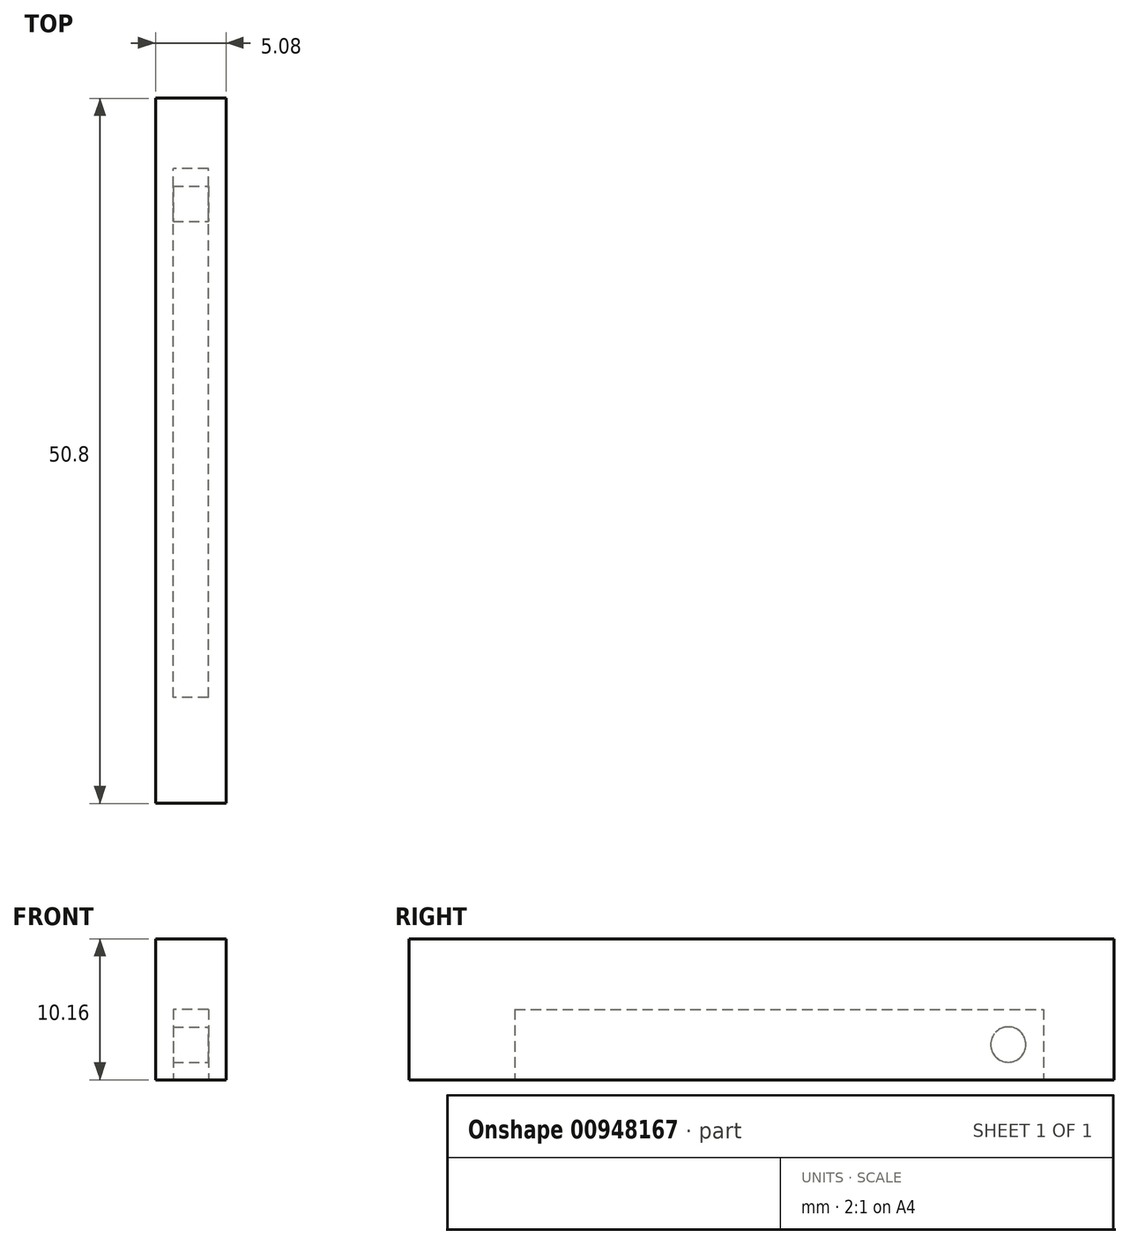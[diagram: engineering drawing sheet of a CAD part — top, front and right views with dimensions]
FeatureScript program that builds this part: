
annotation { "Feature Type Name" : "Feature", "Feature Type Description" : "" }
export const myFeature = defineFeature(function(context is Context, id is Id, definition is map)
    precondition{}
    {
        {
            var Q0;
            Q0=qCreatedBy(makeId("Top.planeOp"),FACE);
            var sketch = newSketch(context, id + "F0", { "sketchPlane" : qUnion([Q0])});
            skLineSegment(sketch, "E0.bottom", {"start": v(-14.1, 25.66) * mm, "end": v(-9.02, 25.66) * mm});
            skLineSegment(sketch, "E0.top", {"start": v(-14.1, -25.14) * mm, "end": v(-9.02, -25.14) * mm});
            skLineSegment(sketch, "E0.left", {"start": v(-14.1, 25.66) * mm, "end": v(-14.1, -25.14) * mm});
            skLineSegment(sketch, "E0.right", {"start": v(-9.02, 25.66) * mm, "end": v(-9.02, -25.14) * mm});
            skLineSegment(sketch, "E1.bottom", {"start": v(-10.3, -17.52) * mm, "end": v(-12.83, -17.52) * mm});
            skLineSegment(sketch, "E1.top", {"start": v(-10.3, 20.58) * mm, "end": v(-12.83, 20.58) * mm});
            skLineSegment(sketch, "E1.left", {"start": v(-10.3, -17.52) * mm, "end": v(-10.3, 20.58) * mm});
            skLineSegment(sketch, "E1.right", {"start": v(-12.83, -17.52) * mm, "end": v(-12.83, 20.58) * mm});
            skPoint(sketch, "E1.middle", {"position": v(-11.56, 1.53) * mm});
            skPoint(sketch, "E1.middle.positionSnap0", {"position": v(-11.56, 25.66) * mm});
            skPoint(sketch, "E1.centerSnap0", {"position": v(-11.56, 25.66) * mm});
            skSolve(sketch);
        }
        {
            var Q0;
            Q0=makeQuery(id+"F0.imprint","IMPRINT",FACE,{"disambiguationData":[TD([[makeQuery(id+"F0.imprint","IMPRINT",EDGE,{"derivedFrom":sQuery(id+"F0.wireOp",EDGE,"E0.bottom")}),-1.0]])]});
            var Q1;
            Q1=makeQuery(id+"F0.imprint","IMPRINT",FACE,{"disambiguationData":[TD([[makeQuery(id+"F0.imprint","IMPRINT",EDGE,{"derivedFrom":sQuery(id+"F0.wireOp",EDGE,"E1.bottom")}),-1.0]])]});
            extrude(context, id + "F1", {"entities" : qUnion([Q0, Q1]), "depth" : 10.16 * mm, "offsetDistance" : 25.4 * mm});
        }
        {
            var Q0;
            Q0=makeQuery(id+"F0.imprint","IMPRINT",FACE,{"disambiguationData":[TD([[makeQuery(id+"F0.imprint","IMPRINT",EDGE,{"derivedFrom":sQuery(id+"F0.wireOp",EDGE,"E1.bottom")}),-1.0]])]});
            extrude(context, id + "F2", {"entities" : qUnion([Q0]), "operationType" : NewBodyOperationType.REMOVE, "depth" : 5.08 * mm, "offsetDistance" : 25.4 * mm});
        }
        {
            var Q0;
            Q0=makeQuery(id+"F2.boolean.opBoolean","COPY",FACE,{"derivedFrom":makeQuery(id+"F2.opExtrude","SWEPT_FACE",FACE,{"disambiguationData":[OSD([sQuery(id+"F0.wireOp",EDGE,"E1.left")])]})});
            var sketch = newSketch(context, id + "F3", { "sketchPlane" : qUnion([Q0])});
            skCircle(sketch, "E2", {"center": v(-18.04, 2.54) * mm, "radius": 1.27 * mm});
            skPoint(sketch, "E2.centerSnap0", {"position": v(-20.58, 2.54) * mm});
            skSolve(sketch);
        }
        {
            var Q0;
            Q0=makeQuery(id+"F3.imprint","IMPRINT",FACE,{"disambiguationData":[TD([[makeQuery(id+"F3.imprint","IMPRINT",EDGE,{"derivedFrom":sQuery(id+"F3.wireOp",EDGE,"E2")}),1.0]])]});
            extrude(context, id + "F4", {"entities" : qUnion([Q0]), "operationType" : NewBodyOperationType.ADD, "depth" : 2.54 * mm, "offsetDistance" : 25.4 * mm});
        }
    });
